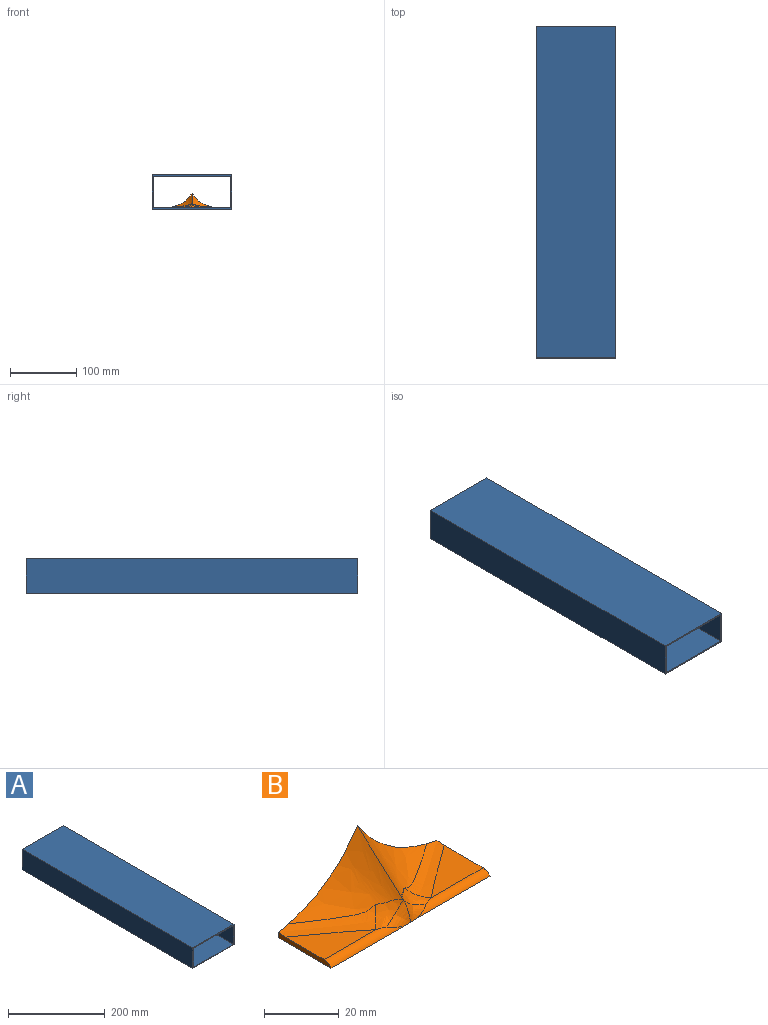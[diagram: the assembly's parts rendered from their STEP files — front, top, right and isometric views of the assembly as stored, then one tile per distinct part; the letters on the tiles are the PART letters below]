
ASSEMBLY  parts=2 mates=1
PART A: 10 faces, bbox 120x500x52 mm
  f0: plane 500x48mm, normal (1,0,0), area 24000mm2, adj f1,f3,f6,f9
  f1: plane 120x52mm, normal (0,-1,0), area 672mm2, adj f0,f2,f4,f5,f6,f7,f8,f9
  f2: plane 500x52mm, normal (1,0,0), area 26000mm2, adj f1,f3,f5,f7
  f3: plane 120x52mm, normal (0,1,0), area 672mm2, adj f0,f2,f4,f5,f6,f7,f8,f9
  f4: plane 500x52mm, normal (-1,0,0), area 26000mm2, adj f1,f3,f5,f7
  f5: plane 500x120mm, normal (0,0,-1), area 60000mm2, adj f1,f2,f3,f4
  f6: plane 500x116mm, normal (0,0,1), area 58000mm2, adj f0,f1,f3,f8
  f7: plane 500x120mm, normal (0,0,1), area 60000mm2, adj f1,f2,f3,f4
  f8: plane 500x48mm, normal (-1,0,0), area 24000mm2, adj f1,f3,f6,f9
  f9: plane 500x116mm, normal (0,0,-1), area 58000mm2, adj f0,f1,f3,f8
PART B: 18 faces, bbox 67.4x23.8x22.2 mm
  f0: plane 60.03x21.53mm, normal (0,1,0), area 512.1mm2, adj f1,f3,f4,f7,f10,f12,f15
  f1: bspline ~30x20mm, area 329.1mm2, adj f0,f2,f7,f8,f10
  f2: bspline ~4.01x2.83mm, area 0mm2, adj f1,f9,f11
  f3: plane 20.01x1.76mm, normal (1,0,0), area 29.1mm2, adj f0,f4,f5,f6,f7
  f4: plane 60.05x20.15mm, normal (0,0,-1), area 1200.2mm2, adj f0,f3,f6,f9,f12,f14,f17
  f5: plane 19.51x14.68mm, normal (0,0,1), area 146.7mm2, adj f3,f6,f7
  f6: cylinder r=3mm len=27.18mm, axis (1,0,0), area 74.1mm2, adj f3,f4,f5,f8,f9
  f7: bspline ~28.68x21.18mm, area 131.4mm2, adj f0,f1,f3,f5,f8
  f8: bspline ~10.7x6.3mm, area 39.2mm2, adj f1,f6,f7,f9
  f9: bspline ~9.11x6.7mm, area 27mm2, adj f2,f4,f6,f8,f17
  f10: bspline ~30x20mm, area 329.2mm2, adj f0,f1,f11,f15,f16
  f11: bspline ~4.99x4.44mm, area 0mm2, adj f2,f10,f17
  f12: plane 20.01x1.76mm, normal (-1,0,0), area 29.1mm2, adj f0,f4,f13,f14,f15
  f13: plane 19.51x14.68mm, normal (0,0,1), area 146.7mm2, adj f12,f14,f15
  f14: cylinder r=3mm len=27.18mm, axis (-1,0,0), area 74.1mm2, adj f4,f12,f13,f16,f17
  f15: bspline ~28.68x21.18mm, area 131.4mm2, adj f0,f10,f12,f13,f16
  f16: bspline ~10.52x6.15mm, area 39.2mm2, adj f10,f14,f15,f17
  f17: bspline ~9.11x6.7mm, area 27mm2, adj f4,f9,f11,f14,f16
PLACE A t=(0,98.16,0.5)mm
PLACE B at identity
MATE slider A.f6 <-> B.f4  axis (0,0,1) through (0,100,-1.5)mm
